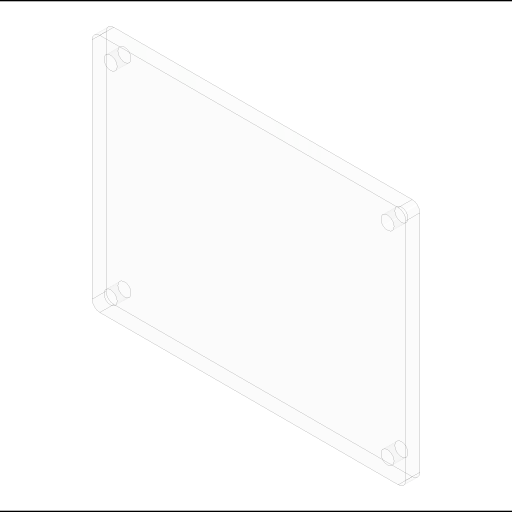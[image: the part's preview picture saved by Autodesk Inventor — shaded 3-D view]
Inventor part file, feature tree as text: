
AUTODESK INVENTOR PART (.ipt)
format: ipt  version: 2023 (Build 270158000, 158)  size: 115,712 bytes
history: native  units: in
note: dims shown in document units (in); Inventor stores cm internally (conversion verified against a paired STEP export)
features: extrude x2, sketch x2, fillet x1
ambient origin geometry x8: Origin, YZ Plane, XZ Plane, XY Plane, X Axis, Y Axis, Z Axis, Center Point
bodies: Solid1 (feature_tree)
feature tree (5):
  extrude  "Extrusion1"  Depth=3.9075in
  fillet  "Fillet1"  Radius=0.227in
  extrude  "Extrusion2"  Depth=0.125in
  sketch  "Sketch1"  dims[d0=5.1075in d1=3.9075in d2=0.227in d3=0.0in]
  sketch  "Sketch2"  dims[d4=0.125in d5=0.3in d6=0.3in d7=0.3in d8=0.3in d9=0.3in d10=0.3in d11=0.217in d12=0.217in d13=0.217in d14=0.3in d15=0.3in d16=0.217in d17=0.0in d18=0.0in]
